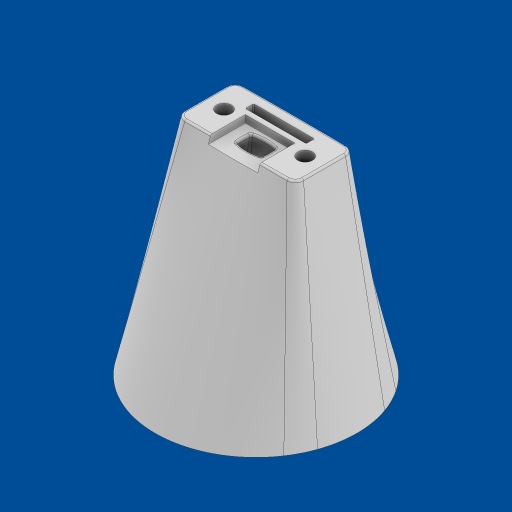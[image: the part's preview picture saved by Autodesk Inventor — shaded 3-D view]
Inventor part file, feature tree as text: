
AUTODESK INVENTOR PART (.ipt)
format: ipt  version: 2023.2 (Build 272271000, 271)  size: 590,336 bytes
history: native  units: mm
features: sketch x4, plane x2, loft x2, extrude x2, hole x1, fillet x1, other x1
ambient origin geometry x8: Origin, YZ Plane, XZ Plane, XY Plane, X Axis, Y Axis, Z Axis, Center Point
bodies: Solid1 (feature_tree)
feature tree (13):
  sketch  "Sketch1"  dims[d3=2.54mm d32=3.0mm]
  plane  "Work Plane1"
  plane  "Work Plane2"
  sketch  "Sketch3"  dims[d98=2.0mm d100=15.439432mm]
  sketch  "Sketch2"  dims[d38=1.0mm d95=3.0mm]
  loft  "Loft1"
  loft  "Loft2"
  hole  "Hole1"  [1 undecoded]
  extrude  "Extrusion1"  Depth=19.687651mm
  extrude  "Extrusion2"  Depth=3.746814mm
  fillet  "Fillet2"  Radius=2.004073mm
  other  "Image2"
  sketch  "Sketch4"  dims[d102=10.117381mm d103=19.687651mm d104=3.746814mm d105=2.004073mm d106=14.738579mm d108=0.034664mm d109=2.839811mm d110=4.849079mm d111=0.520217mm d112=2.280245mm d114=5.218519mm d116=7.717951mm d123=2.0mm d124=3.0mm d125=-50.0mm d126=50.0mm d127=3.054326mm d128=2.181662mm d129=34.529879mm d130=34.925mm d131=7.0mm d132=2.0mm d133=0.25mm d134=0.0mm d135=90.0deg d136=0.0mm d137=90.0deg d138=0.0mm d139=90.0deg d140=0.0mm d141=90.0deg d142=3.571875mm d143=6.0mm d144=4.0mm d145=2.0mm d146=90.0deg d147=6.5mm d148=0.0mm d149=2.0mm d150=0.0mm d153=2.0mm d154=12.0mm d155=1.75mm d156=0.0mm d157=0.5mm]
note: 1 required parameter value undecoded (feature->parameter linkage not recoverable at this tier; creation-order binding heuristic only, values carry confidence <= 0.55)
